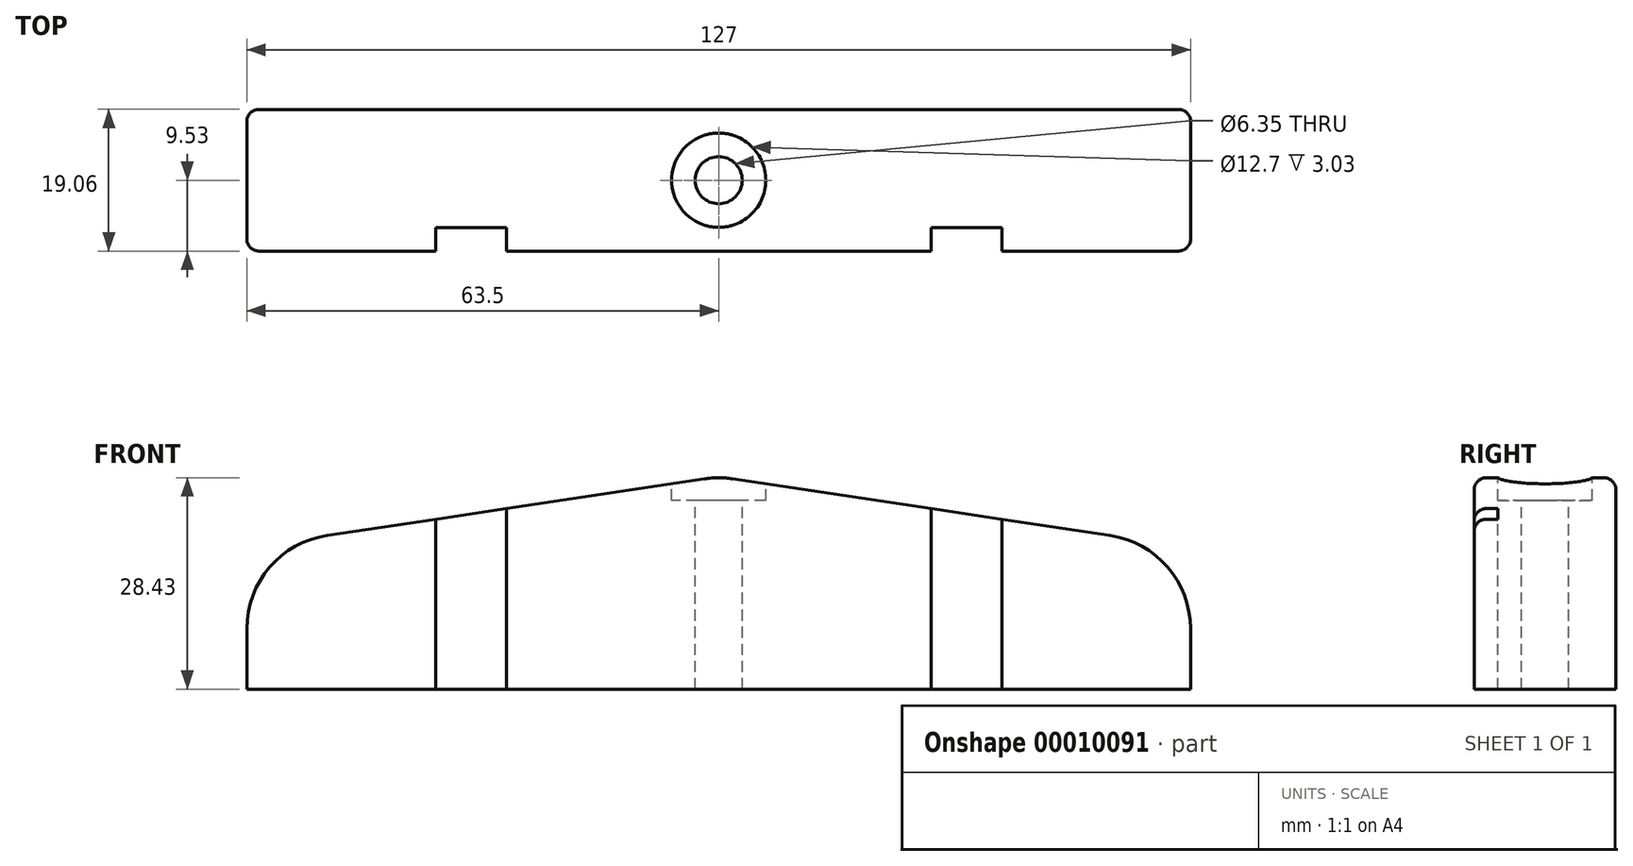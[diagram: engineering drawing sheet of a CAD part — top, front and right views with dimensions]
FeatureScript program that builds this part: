
annotation { "Feature Type Name" : "Feature", "Feature Type Description" : "" }
export const myFeature = defineFeature(function(context is Context, id is Id, definition is map)
    precondition{}
    {
        {
            var Q0;
            Q0=qCreatedBy(makeId("Front.planeOp"),FACE);
            var sketch = newSketch(context, id + "F0", { "sketchPlane" : qUnion([Q0])});
            skLineSegment(sketch, "E0", {"start": v(0, 0) * mm, "end": v(63.5, 0) * mm});
            skLineSegment(sketch, "E1", {"start": v(63.5, 0) * mm, "end": v(63.5, 8.11) * mm});
            skLineSegment(sketch, "E2", {"start": v(-15.96, 28.58) * mm, "end": v(23.13, 28.58) * mm, "construction": true});
            skPoint(sketch, "E3.end.orphan", {"position": v(0, 23.87) * mm});
            skLineSegment(sketch, "E4", {"start": v(52.68, 20.67) * mm, "end": v(1.88, 28.3) * mm});
            skLineSegment(sketch, "E5", {"start": v(0, 54.2) * mm, "end": v(0, -37.29) * mm, "construction": true});
            skLineSegment(sketch, "E6.0.MirrorCS", {"start": v(0, 0) * mm, "end": v(-63.5, 0) * mm});
            skLineSegment(sketch, "E6.1.MirrorCS", {"start": v(-52.68, 20.67) * mm, "end": v(-1.88, 28.3) * mm});
            skLineSegment(sketch, "E6.2.MirrorCS", {"start": v(-63.5, 0) * mm, "end": v(-63.5, 8.11) * mm});
            skLineSegment(sketch, "E6.3.MirrorCS", {"start": v(15.96, 28.58) * mm, "end": v(-23.13, 28.58) * mm, "construction": true});
            skPoint(sketch, "E7.visualSharp", {"position": v(0, 28.58) * mm});
            skArc(sketch, "E7.filletArc", {"start": v(1.88, 28.3) * mm, "mid": v(0, 28.43) * mm, "end": v(-1.88, 28.3) * mm});
            skPoint(sketch, "E8.visualSharp", {"position": v(63.5, 19.05) * mm});
            skArc(sketch, "E8.filletArc", {"start": v(63.5, 8.11) * mm, "mid": v(60.42, 16.4) * mm, "end": v(52.68, 20.67) * mm});
            skPoint(sketch, "E9.visualSharp", {"position": v(-63.5, 19.05) * mm});
            skArc(sketch, "E9.filletArc", {"start": v(-52.68, 20.67) * mm, "mid": v(-60.42, 16.4) * mm, "end": v(-63.5, 8.11) * mm});
            skSolve(sketch);
        }
        {
            var Q0;
            Q0=makeQuery(id+"F0.imprint","IMPRINT",FACE,{"disambiguationData":[TD([[makeQuery(id+"F0.imprint","IMPRINT",EDGE,{"derivedFrom":sQuery(id+"F0.wireOp",EDGE,"E0")}),1.0]])]});
            extrude(context, id + "F1", {"entities" : qUnion([Q0]), "endBound" : BoundingType.SYMMETRIC, "oppositeDirection" : true, "depth" : 19.05 * mm});
        }
        {
            var Q0;
            Q0=qCreatedBy(makeId("Top.planeOp"),FACE);
            cPlane(context, id + "F2", {"entities" : qUnion([Q0]), "cplaneType" : CPlaneType.OFFSET, "offset" : 28.57 * mm, "width" : 152.4 * mm, "height" : 152.4 * mm});
        }
        {
            var Q0;
            Q0=qCreatedBy(id+"F2.planeOp",FACE);
            var sketch = newSketch(context, id + "F3", { "sketchPlane" : qUnion([Q0])});
            skCircle(sketch, "E10", {"center": v(0, 0) * mm, "radius": 6.35 * mm});
            skCircle(sketch, "E11", {"center": v(0, 0) * mm, "radius": 3.18 * mm});
            skSolve(sketch);
        }
        {
            var Q0;
            Q0=makeQuery(id+"F3.imprint","IMPRINT",FACE,{"disambiguationData":[TD([[makeQuery(id+"F3.imprint","IMPRINT",EDGE,{"derivedFrom":sQuery(id+"F3.wireOp",EDGE,"E11")}),1.0]])]});
            var Q1;
            Q1=sQuery(id+"F3.wireOp",EDGE,"E11");
            extrude(context, id + "F4", {"entities" : qUnion([Q0]), "operationType" : NewBodyOperationType.REMOVE, "surfaceEntities" : qUnion([Q1]), "endBound" : BoundingType.THROUGH_ALL, "oppositeDirection" : true, "depth" : 25.4 * mm});
        }
        {
            var Q0;
            Q0 = qSketchRegion(id + "F3", true);
            extrude(context, id + "F5", {"entities" : qUnion([Q0]), "operationType" : NewBodyOperationType.REMOVE, "oppositeDirection" : true, "depth" : 3.17 * mm});
        }
        {
            var Q0;
            Q0=makeQuery(id+"F1.opExtrude","CAP_EDGE",EDGE,{"disambiguationData":[OSD([sQuery(id+"F0.wireOp",EDGE,"E1")])],"isStart":true});
            var Q1;
            Q1=makeQuery(id+"F1.opExtrude","CAP_EDGE",EDGE,{"disambiguationData":[OSD([sQuery(id+"F0.wireOp",EDGE,"E8.filletArc")])],"isStart":true});
            var Q2;
            Q2=makeQuery(id+"F1.opExtrude","CAP_EDGE",EDGE,{"disambiguationData":[OSD([sQuery(id+"F0.wireOp",EDGE,"E4")])],"isStart":true});
            var Q3;
            Q3=makeQuery(id+"F1.opExtrude","CAP_EDGE",EDGE,{"disambiguationData":[OSD([sQuery(id+"F0.wireOp",EDGE,"E7.filletArc")])],"isStart":true});
            var Q4;
            Q4=makeQuery(id+"F1.opExtrude","CAP_EDGE",EDGE,{"disambiguationData":[OSD([sQuery(id+"F0.wireOp",EDGE,"E6.1.MirrorCS")])],"isStart":true});
            var Q5;
            Q5=makeQuery(id+"F1.opExtrude","CAP_EDGE",EDGE,{"disambiguationData":[OSD([sQuery(id+"F0.wireOp",EDGE,"E9.filletArc")])],"isStart":true});
            var Q6;
            Q6=makeQuery(id+"F1.opExtrude","CAP_EDGE",EDGE,{"disambiguationData":[OSD([sQuery(id+"F0.wireOp",EDGE,"E6.2.MirrorCS")])],"isStart":true});
            var Q7;
            Q7=makeQuery(id+"F1.opExtrude","CAP_EDGE",EDGE,{"disambiguationData":[OSD([sQuery(id+"F0.wireOp",EDGE,"E6.2.MirrorCS")])],"isStart":false});
            var Q8;
            Q8=makeQuery(id+"F1.opExtrude","CAP_EDGE",EDGE,{"disambiguationData":[OSD([sQuery(id+"F0.wireOp",EDGE,"E9.filletArc")])],"isStart":false});
            var Q9;
            Q9=makeQuery(id+"F1.opExtrude","CAP_EDGE",EDGE,{"disambiguationData":[OSD([sQuery(id+"F0.wireOp",EDGE,"E6.1.MirrorCS")])],"isStart":false});
            var Q10;
            Q10=makeQuery(id+"F1.opExtrude","CAP_EDGE",EDGE,{"disambiguationData":[OSD([sQuery(id+"F0.wireOp",EDGE,"E7.filletArc")])],"isStart":false});
            var Q11;
            Q11=makeQuery(id+"F1.opExtrude","CAP_EDGE",EDGE,{"disambiguationData":[OSD([sQuery(id+"F0.wireOp",EDGE,"E8.filletArc")])],"isStart":false});
            var Q12;
            Q12=makeQuery(id+"F1.opExtrude","CAP_EDGE",EDGE,{"disambiguationData":[OSD([sQuery(id+"F0.wireOp",EDGE,"E1")])],"isStart":false});
            var Q13;
            Q13=makeQuery(id+"F1.opExtrude","CAP_EDGE",EDGE,{"disambiguationData":[OSD([sQuery(id+"F0.wireOp",EDGE,"E4")])],"isStart":false});
            fillet(context, id + "F6", {"entities" : qUnion([Q0, Q1, Q2, Q3, Q4, Q5, Q6, Q7, Q8, Q9, Q10, Q11, Q12, Q13]), "radius" : 1.59 * mm, "allowEdgeOverflow" : false});
        }
        {
            var Q0;
            Q0=makeQuery(id+"F1.opExtrude","CAP_FACE",FACE,{"disambiguationData":[OSD([sQuery(id+"F0.wireOp",EDGE,"E0"),sQuery(id+"F0.wireOp",EDGE,"E1"),sQuery(id+"F0.wireOp",EDGE,"E4"),sQuery(id+"F0.wireOp",EDGE,"E6.0.MirrorCS"),sQuery(id+"F0.wireOp",EDGE,"E6.1.MirrorCS"),sQuery(id+"F0.wireOp",EDGE,"E6.2.MirrorCS"),sQuery(id+"F0.wireOp",EDGE,"E7.filletArc"),sQuery(id+"F0.wireOp",EDGE,"E8.filletArc"),sQuery(id+"F0.wireOp",EDGE,"E9.filletArc")])],"isStart":true});
            var sketch = newSketch(context, id + "F7", { "sketchPlane" : qUnion([Q0])});
            skLineSegment(sketch, "E12", {"start": v(0, 0) * mm, "end": v(0, 39.84) * mm, "construction": true});
            skLineSegment(sketch, "E13.bottom", {"start": v(-38.1, 0) * mm, "end": v(-28.57, 0) * mm});
            skLineSegment(sketch, "E13.top", {"start": v(-38.1, 28.58) * mm, "end": v(-28.57, 28.58) * mm});
            skLineSegment(sketch, "E13.left", {"start": v(-38.1, 0) * mm, "end": v(-38.1, 28.58) * mm});
            skLineSegment(sketch, "E13.right", {"start": v(-28.57, 0) * mm, "end": v(-28.57, 28.58) * mm});
            skLineSegment(sketch, "E14.MirrorCS", {"start": v(38.1, 0) * mm, "end": v(28.57, 0) * mm});
            skLineSegment(sketch, "E15.MirrorCS", {"start": v(38.1, 28.58) * mm, "end": v(28.57, 28.58) * mm});
            skLineSegment(sketch, "E16.MirrorCS", {"start": v(28.57, 0) * mm, "end": v(28.57, 28.58) * mm});
            skLineSegment(sketch, "E17.MirrorCS", {"start": v(38.1, 0) * mm, "end": v(38.1, 28.58) * mm});
            skSolve(sketch);
        }
        {
            var Q0;
            Q0 = qSketchRegion(id + "F7", true);
            extrude(context, id + "F8", {"entities" : qUnion([Q0]), "operationType" : NewBodyOperationType.REMOVE, "oppositeDirection" : true, "depth" : 3.17 * mm});
        }
    });
